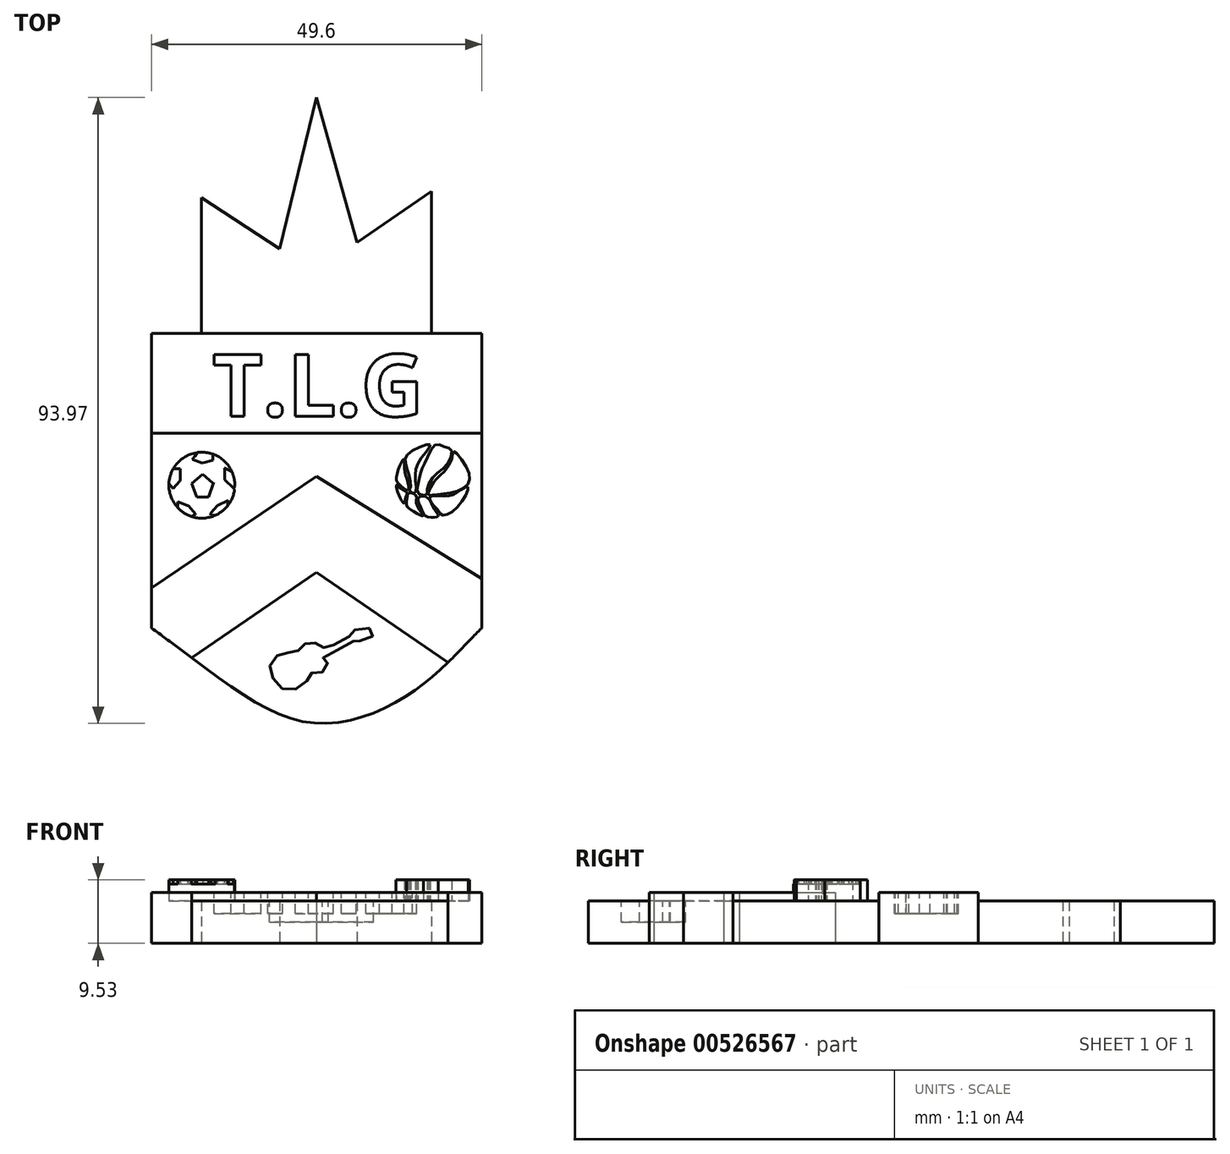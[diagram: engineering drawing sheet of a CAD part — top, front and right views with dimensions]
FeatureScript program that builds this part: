
annotation { "Feature Type Name" : "Feature", "Feature Type Description" : "" }
export const myFeature = defineFeature(function(context is Context, id is Id, definition is map)
    precondition{}
    {
        {
            var Q0;
            Q0=qCreatedBy(makeId("Top.planeOp"),FACE);
            var sketch = newSketch(context, id + "F0", { "sketchPlane" : qUnion([Q0])});
            skLineSegment(sketch, "E0", {"start": v(-64.18, 26.2) * mm, "end": v(-14.58, 26.2) * mm});
            skLineSegment(sketch, "E1", {"start": v(-64.18, 26.2) * mm, "end": v(-64.18, -18.06) * mm});
            skLineSegment(sketch, "E2", {"start": v(-14.58, 26.2) * mm, "end": v(-14.58, -18.06) * mm});
            skFitSpline(sketch, "E3", {"points": [v(-64.18, -18.06) * mm, v(-40.58, -32.23) * mm, v(-24.34, -27.25) * mm, v(-14.58, -18.06) * mm], "startDerivative": vector(70.37, -50.03) * mm, "endDerivative": vector(33.11, 32.24) * mm});
            skLineSegment(sketch, "E4", {"start": v(-64.18, -12.04) * mm, "end": v(-39.43, 4.71) * mm});
            skLineSegment(sketch, "E5", {"start": v(-14.58, -10.64) * mm, "end": v(-39.43, 4.71) * mm});
            skLineSegment(sketch, "E6", {"start": v(-58.11, -22.54) * mm, "end": v(-39.43, -9.71) * mm});
            skLineSegment(sketch, "E7", {"start": v(-39.43, -9.71) * mm, "end": v(-19.66, -23.24) * mm});
            skLineSegment(sketch, "E8", {"start": v(-64.18, 11.22) * mm, "end": v(-14.58, 11.22) * mm});
            skLineSegment(sketch, "E9", {"start": v(-56.7, 26.2) * mm, "end": v(-56.7, 47.49) * mm});
            skLineSegment(sketch, "E10", {"start": v(-58.14, 47.49) * mm, "end": v(-44.93, 38.9) * mm});
            skLineSegment(sketch, "E11", {"start": v(-44.93, 38.9) * mm, "end": v(-39.43, 61.6) * mm});
            skLineSegment(sketch, "E12", {"start": v(-39.43, 61.6) * mm, "end": v(-33.3, 39.83) * mm});
            skLineSegment(sketch, "E13", {"start": v(-33.3, 39.83) * mm, "end": v(-22.14, 47.49) * mm});
            skLineSegment(sketch, "E14", {"start": v(-22.14, 47.49) * mm, "end": v(-22.14, 26.2) * mm});
            skSolve(sketch);
        }
        {
            var Q0;
            {var subQ1=sQuery(id+"F0.wireOp",EDGE,"E4");Q0=makeQuery(id+"F0.imprint","IMPRINT",FACE,{"disambiguationData":[TD([[makeQuery(id+"F0.imprint","IMPRINT",EDGE,{"derivedFrom":subQ1}),1.0]])]});}
            var Q1;
            {var subQ0=sQuery(id+"F0.wireOp",EDGE,"E6");Q1=makeQuery(id+"F0.imprint","IMPRINT",FACE,{"disambiguationData":[TD([[makeQuery(id+"F0.imprint","IMPRINT",EDGE,{"derivedFrom":subQ0}),-1.0]])]});}
            var Q2;
            {var subQ0=sQuery(id+"F0.wireOp",EDGE,"E11");Q2=makeQuery(id+"F0.imprint","IMPRINT",FACE,{"disambiguationData":[TD([[makeQuery(id+"F0.imprint","IMPRINT",EDGE,{"derivedFrom":subQ0}),-1.0]])]});}
            extrude(context, id + "F1", {"entities" : qUnion([Q0, Q1, Q2]), "depth" : 6.35 * mm, "offsetDistance" : 25.4 * mm});
        }
        {
            var Q0;
            Q0=makeQuery(id+"F1.opExtrude","CAP_FACE",FACE,{"disambiguationData":[OSD([sQuery(id+"F0.wireOp",EDGE,"E1"),sQuery(id+"F0.wireOp",EDGE,"E2"),sQuery(id+"F0.wireOp",EDGE,"E4"),sQuery(id+"F0.wireOp",EDGE,"E5"),sQuery(id+"F0.wireOp",EDGE,"E8")])],"isStart":false});
            var sketch = newSketch(context, id + "F2", { "sketchPlane" : qUnion([Q0])});
            skFitSpline(sketch, "E15", {"points": [v(-22.34, 9.48) * mm, v(-25.54, 8.17) * mm, v(-25.95, 6.46) * mm, v(-25.24, 3.28) * mm, v(-25.4, 2.5) * mm, v(-24.6, 2.23) * mm, v(-24.56, 4.4) * mm, v(-23.73, 7.36) * mm, v(-22.34, 9.48) * mm]});
            skFitSpline(sketch, "E16", {"points": [v(-20.21, 9.17) * mm, v(-21.5, 9.48) * mm, v(-22.88, 7.24) * mm, v(-23.68, 5.5) * mm, v(-24.1, 3.57) * mm, v(-24.15, 2.16) * mm, v(-22.9, 1.91) * mm, v(-22.75, 2.8) * mm, v(-21.68, 4.82) * mm, v(-19.75, 6.6) * mm, v(-19.16, 8.7) * mm, v(-20.21, 9.17) * mm]});
            skFitSpline(sketch, "E17", {"points": [v(-18.82, 8.46) * mm, v(-19.04, 7.29) * mm, v(-20.87, 4.8) * mm, v(-21.97, 3.62) * mm, v(-22.58, 1.96) * mm, v(-21.87, 1.91) * mm, v(-19.24, 2.25) * mm, v(-16.65, 3.55) * mm, v(-16.84, 6.04) * mm, v(-18.82, 8.46) * mm]});
            skFitSpline(sketch, "E18", {"points": [v(-22.34, 1.64) * mm, v(-20.02, 1.74) * mm, v(-18.36, 2.25) * mm, v(-16.7, 3.1) * mm, v(-18, 0.35) * mm, v(-20.53, -1.12) * mm, v(-21.02, -0.55) * mm, v(-21.85, 0.37) * mm, v(-22.34, 1.64) * mm]});
            skFitSpline(sketch, "E19", {"points": [v(-24.12, 1.5) * mm, v(-23.49, -0.46) * mm, v(-22.9, -1.29) * mm, v(-21.14, -1.29) * mm, v(-21.7, -0.21) * mm, v(-22.78, 1.52) * mm, v(-24.12, 1.5) * mm]});
            skFitSpline(sketch, "E20", {"points": [v(-25.54, 2.23) * mm, v(-25.78, 1.5) * mm, v(-25.83, 0.3) * mm, v(-24.78, -0.58) * mm, v(-23.36, -1.21) * mm, v(-24.34, 0.52) * mm, v(-24.46, 1.84) * mm, v(-25.54, 2.23) * mm]});
            skFitSpline(sketch, "E21", {"points": [v(-27.42, 3.38) * mm, v(-26.8, 1.5) * mm, v(-26.22, 0.67) * mm, v(-26, 1.6) * mm, v(-25.82, 2.33) * mm, v(-27.1, 3.2) * mm, v(-27.28, 3.45) * mm, v(-27.42, 3.38) * mm]});
            skFitSpline(sketch, "E22", {"points": [v(-25.67, 2.6) * mm, v(-26.82, 3.38) * mm, v(-27.38, 4.1) * mm, v(-27, 6.04) * mm, v(-26.28, 7.28) * mm, v(-26.18, 5.84) * mm, v(-25.68, 3.82) * mm, v(-25.67, 2.6) * mm]});
            skSolve(sketch);
        }
        {
            var Q0;
            {var subQ3=sQuery(id+"F0.wireOp",EDGE,"E8");Q0=makeQuery(id+"F0.imprint","IMPRINT",FACE,{"disambiguationData":[TD([[makeQuery(id+"F0.imprint","IMPRINT",EDGE,{"derivedFrom":subQ3}),1.0]])]});}
            var Q1;
            {var subQ8=sQuery(id+"F0.wireOp",EDGE,"E4");Q1=makeQuery(id+"F0.imprint","IMPRINT",FACE,{"disambiguationData":[TD([[makeQuery(id+"F0.imprint","IMPRINT",EDGE,{"derivedFrom":subQ8}),-1.0]])]});}
            var Q2;
            Q2=sQuery(id+"F0.wireOp",EDGE,"E9");
            var Q3;
            Q3=sQuery(id+"F0.wireOp",EDGE,"E7");
            var Q4;
            Q4=sQuery(id+"F0.wireOp",EDGE,"E5");
            var Q5;
            Q5=sQuery(id+"F0.wireOp",EDGE,"E4");
            var Q6;
            Q6=sQuery(id+"F0.wireOp",EDGE,"E3");
            var Q7;
            Q7=sQuery(id+"F0.wireOp",EDGE,"E2");
            var Q8;
            Q8=sQuery(id+"F0.wireOp",EDGE,"E1");
            var Q9;
            Q9=sQuery(id+"F0.wireOp",EDGE,"E0");
            var Q10;
            Q10=sQuery(id+"F0.wireOp",EDGE,"E14");
            var Q11;
            Q11=sQuery(id+"F0.wireOp",EDGE,"E13");
            var Q12;
            Q12=sQuery(id+"F0.wireOp",EDGE,"E12");
            var Q13;
            Q13=sQuery(id+"F0.wireOp",EDGE,"E11");
            extrude(context, id + "F3", {"entities" : qUnion([Q0, Q1]), "surfaceEntities" : qUnion([Q2, Q3, Q4, Q5, Q6, Q7, Q8, Q9, Q10, Q11, Q12, Q13]), "depth" : 7.62 * mm, "offsetDistance" : 25.4 * mm});
        }
        {
            var Q0;
            Q0=makeQuery(id+"F3.opExtrude","CAP_FACE",FACE,{"disambiguationData":[OSD([sQuery(id+"F0.wireOp",EDGE,"E0"),sQuery(id+"F0.wireOp",EDGE,"E1"),sQuery(id+"F0.wireOp",EDGE,"E2"),sQuery(id+"F0.wireOp",EDGE,"E8")])],"isStart":false});
            var sketch = newSketch(context, id + "F4", { "sketchPlane" : qUnion([Q0])});
            skText(sketch, "E23", { "text": "T.L.G", "fontName": "OpenSans-Bold.ttf"});
            const initialGuessF4  = {"E23": [-0.055, 0.01375, 1, 0, 0.00936]};
            skSetInitialGuess(sketch, initialGuessF4);
            skSolve(sketch);
        }
        {
            var Q0;
            Q0 = qSketchRegion(id + "F4", true);
            extrude(context, id + "F5", {"entities" : qUnion([Q0]), "operationType" : NewBodyOperationType.REMOVE, "depth" : 3.17 * mm, "offsetDistance" : 25.4 * mm});
        }
        {
            var Q0;
            Q0 = qSketchRegion(id + "F4", true);
            extrude(context, id + "F6", {"entities" : qUnion([Q0]), "operationType" : NewBodyOperationType.REMOVE, "oppositeDirection" : true, "depth" : 3.17 * mm, "offsetDistance" : 25.4 * mm});
        }
        {
            var Q0;
            Q0=makeQuery(id+"F1.opExtrude","CAP_FACE",FACE,{"disambiguationData":[OSD([sQuery(id+"F0.wireOp",EDGE,"E1"),sQuery(id+"F0.wireOp",EDGE,"E2"),sQuery(id+"F0.wireOp",EDGE,"E4"),sQuery(id+"F0.wireOp",EDGE,"E5"),sQuery(id+"F0.wireOp",EDGE,"E8")])],"isStart":false});
            var sketch = newSketch(context, id + "F7", { "sketchPlane" : qUnion([Q0])});
            skCircle(sketch, "E24", {"center": v(-56.6, 3.39) * mm, "radius": 4.95 * mm});
            skLineSegment(sketch, "E25", {"start": v(-56.48, 5.06) * mm, "end": v(-58.18, 3.6) * mm});
            skLineSegment(sketch, "E26", {"start": v(-58.14, 3.68) * mm, "end": v(-57.35, 1.63) * mm});
            skLineSegment(sketch, "E27", {"start": v(-57.43, 1.63) * mm, "end": v(-55.62, 1.63) * mm});
            skLineSegment(sketch, "E28", {"start": v(-55.58, 1.63) * mm, "end": v(-54.83, 3.84) * mm});
            skLineSegment(sketch, "E29", {"start": v(-54.95, 3.72) * mm, "end": v(-56.48, 5.06) * mm});
            skLineSegment(sketch, "E30", {"start": v(-57.65, 7.8) * mm, "end": v(-58.05, 7.28) * mm});
            skLineSegment(sketch, "E31", {"start": v(-58.02, 7.23) * mm, "end": v(-56.48, 6.68) * mm});
            skLineSegment(sketch, "E32", {"start": v(-56.4, 6.72) * mm, "end": v(-54.95, 7.15) * mm});
            skLineSegment(sketch, "E33", {"start": v(-54.97, 7.21) * mm, "end": v(-54.97, 8.06) * mm});
            skLineSegment(sketch, "E34", {"start": v(-57.65, 7.8) * mm, "end": v(-57.32, 8.29) * mm});
            skLineSegment(sketch, "E35", {"start": v(-60.21, -0.01) * mm, "end": v(-60.21, 0.92) * mm});
            skLineSegment(sketch, "E36", {"start": v(-60.21, 0.92) * mm, "end": v(-58.77, 0.33) * mm});
            skLineSegment(sketch, "E37", {"start": v(-58.65, 0.33) * mm, "end": v(-57.59, -0.94) * mm});
            skLineSegment(sketch, "E38", {"start": v(-57.55, -1.01) * mm, "end": v(-58.2, -1.3) * mm});
            skLineSegment(sketch, "E39", {"start": v(-60.91, 5.84) * mm, "end": v(-59.84, 5.84) * mm});
            skLineSegment(sketch, "E40", {"start": v(-59.84, 5.84) * mm, "end": v(-59.84, 4.15) * mm});
            skLineSegment(sketch, "E41", {"start": v(-59.92, 4.04) * mm, "end": v(-60.9, 2.9) * mm});
            skLineSegment(sketch, "E42", {"start": v(-60.9, 2.85) * mm, "end": v(-61.5, 3.56) * mm});
            skLineSegment(sketch, "E43", {"start": v(-52.5, 5.61) * mm, "end": v(-53.25, 6) * mm});
            skLineSegment(sketch, "E44", {"start": v(-53.17, 5.9) * mm, "end": v(-53.17, 4.2) * mm});
            skLineSegment(sketch, "E45", {"start": v(-53.17, 4.2) * mm, "end": v(-51.7, 2.78) * mm});
            skLineSegment(sketch, "E46", {"start": v(-51.99, 2.81) * mm, "end": v(-51.66, 3.24) * mm});
            skLineSegment(sketch, "E47", {"start": v(-54.55, -1.12) * mm, "end": v(-55.26, -1.12) * mm});
            skLineSegment(sketch, "E48", {"start": v(-55.26, -0.82) * mm, "end": v(-54.24, 0.33) * mm});
            skLineSegment(sketch, "E49", {"start": v(-54.24, 0.33) * mm, "end": v(-52.66, 1.08) * mm});
            skLineSegment(sketch, "E50", {"start": v(-52.66, 1.08) * mm, "end": v(-52.74, 0.29) * mm});
            skLineSegment(sketch, "E51", {"start": v(-61.5, 3.56) * mm, "end": v(-61.55, 3.65) * mm});
            skLineSegment(sketch, "E52", {"start": v(-60.9, 2.9) * mm, "end": v(-60.9, 2.85) * mm});
            skLineSegment(sketch, "E53", {"start": v(-59.84, 4.15) * mm, "end": v(-59.92, 4.04) * mm});
            skLineSegment(sketch, "E54", {"start": v(-56.4, 6.72) * mm, "end": v(-56.48, 6.68) * mm});
            skLineSegment(sketch, "E55", {"start": v(-54.97, 7.21) * mm, "end": v(-54.95, 7.15) * mm});
            skLineSegment(sketch, "E56", {"start": v(-58.05, 7.28) * mm, "end": v(-58.02, 7.23) * mm});
            skLineSegment(sketch, "E57", {"start": v(-53.25, 6) * mm, "end": v(-53.17, 5.9) * mm});
            skLineSegment(sketch, "E58", {"start": v(-52.5, 5.61) * mm, "end": v(-52.04, 5.31) * mm});
            skLineSegment(sketch, "E59", {"start": v(-54.95, 3.72) * mm, "end": v(-54.83, 3.84) * mm});
            skLineSegment(sketch, "E60", {"start": v(-55.58, 1.63) * mm, "end": v(-55.62, 1.63) * mm});
            skLineSegment(sketch, "E61", {"start": v(-55.26, -0.82) * mm, "end": v(-55.26, -1.12) * mm});
            skLineSegment(sketch, "E62", {"start": v(-57.59, -0.94) * mm, "end": v(-57.55, -1.01) * mm});
            skLineSegment(sketch, "E63", {"start": v(-58.77, 0.33) * mm, "end": v(-58.65, 0.33) * mm});
            skSolve(sketch);
        }
        {
            var Q0;
            Q0=makeQuery(id+"F7.imprint","IMPRINT",FACE,{"disambiguationData":[TD([[makeQuery(id+"F7.imprint","IMPRINT",EDGE,{"derivedFrom":sQuery(id+"F7.wireOp",EDGE,"E30")}),1.0]])]});
            var Q1;
            Q1=makeQuery(id+"F7.imprint","IMPRINT",FACE,{"disambiguationData":[TD([[makeQuery(id+"F7.imprint","IMPRINT",EDGE,{"derivedFrom":sQuery(id+"F7.wireOp",EDGE,"E28")}),1.0]])]});
            var Q2;
            Q2=makeQuery(id+"F7.imprint","IMPRINT",FACE,{"disambiguationData":[TD([[makeQuery(id+"F7.imprint","IMPRINT",EDGE,{"derivedFrom":sQuery(id+"F7.wireOp",EDGE,"E43")}),1.0]])]});
            var Q3;
            {var subQ1=sQuery(id+"F7.wireOp",EDGE,"E39");Q3=makeQuery(id+"F7.imprint","IMPRINT",FACE,{"disambiguationData":[TD([[makeQuery(id+"F7.imprint","IMPRINT",EDGE,{"derivedFrom":subQ1}),-1.0]])]});}
            var Q4;
            {var subQ0=sQuery(id+"F7.wireOp",EDGE,"E35");Q4=makeQuery(id+"F7.imprint","IMPRINT",FACE,{"disambiguationData":[TD([[makeQuery(id+"F7.imprint","IMPRINT",EDGE,{"derivedFrom":subQ0}),-1.0]])]});}
            var Q5;
            {var subQ1=sQuery(id+"F7.wireOp",EDGE,"E47");Q5=makeQuery(id+"F7.imprint","IMPRINT",FACE,{"disambiguationData":[TD([[makeQuery(id+"F7.imprint","IMPRINT",EDGE,{"derivedFrom":subQ1}),-1.0]])]});}
            extrude(context, id + "F8", {"entities" : qUnion([Q0, Q1, Q2, Q3, Q4, Q5]), "operationType" : NewBodyOperationType.ADD, "depth" : 3.17 * mm, "offsetDistance" : 25.4 * mm});
        }
        {
            var Q0;
            Q0=makeQuery(id+"F7.imprint","IMPRINT",FACE,{"disambiguationData":[TD([[makeQuery(id+"F7.imprint","IMPRINT",EDGE,{"derivedFrom":sQuery(id+"F7.wireOp",EDGE,"E28")}),-1.0]])]});
            extrude(context, id + "F9", {"entities" : qUnion([Q0]), "operationType" : NewBodyOperationType.ADD, "depth" : 2.54 * mm, "offsetDistance" : 25.4 * mm});
        }
        {
            var Q0;
            Q0 = qSketchRegion(id + "F2", true);
            extrude(context, id + "F10", {"entities" : qUnion([Q0]), "depth" : 3.17 * mm, "offsetDistance" : 25.4 * mm});
        }
        {
            var Q0;
            Q0=makeQuery(id+"F1.opExtrude","CAP_FACE",FACE,{"disambiguationData":[OSD([sQuery(id+"F0.wireOp",EDGE,"E3"),sQuery(id+"F0.wireOp",EDGE,"E6"),sQuery(id+"F0.wireOp",EDGE,"E7")])],"isStart":false});
            var sketch = newSketch(context, id + "F11", { "sketchPlane" : qUnion([Q0])});
            skFitSpline(sketch, "E64", {"points": [v(-39.6, -20.28) * mm, v(-40.61, -20.21) * mm, v(-41.5, -20.77) * mm, v(-42, -21.35) * mm, v(-42.61, -21.66) * mm, v(-43.75, -21.77) * mm, v(-44.96, -22.04) * mm, v(-46, -22.87) * mm, v(-46.45, -24.22) * mm, v(-45.86, -25.7) * mm, v(-44.62, -27.09) * mm, v(-42.96, -27.36) * mm, v(-41.34, -26.53) * mm, v(-40.58, -25.43) * mm, v(-40.23, -24.84) * mm, v(-39.1, -24.7) * mm, v(-38.23, -24.53) * mm, v(-37.68, -23.42) * mm, v(-38.33, -23.11) * mm, v(-38.47, -22.63) * mm, v(-37.3, -21.9) * mm, v(-34.05, -20.14) * mm, v(-33.7, -20.04) * mm, v(-33.29, -20.14) * mm, v(-32.11, -19.7) * mm, v(-30.84, -19.14) * mm, v(-31.08, -18.59) * mm, v(-32.11, -17.76) * mm, v(-34.12, -18.8) * mm, v(-34.26, -19.18) * mm, v(-35.33, -19.73) * mm, v(-38.09, -21.18) * mm, v(-38.3, -21.08) * mm, v(-38.54, -20.66) * mm, v(-39.6, -20.28) * mm]});
            skSolve(sketch);
        }
        {
            var Q0;
            Q0=makeQuery(id+"F11.imprint","IMPRINT",FACE,{"disambiguationData":[TD([[makeQuery(id+"F11.imprint","IMPRINT",EDGE,{"derivedFrom":sQuery(id+"F11.wireOp",EDGE,"E64")}),1.0]])]});
            extrude(context, id + "F12", {"entities" : qUnion([Q0]), "operationType" : NewBodyOperationType.REMOVE, "oppositeDirection" : true, "depth" : 3.17 * mm, "offsetDistance" : 25.4 * mm});
        }
    });
